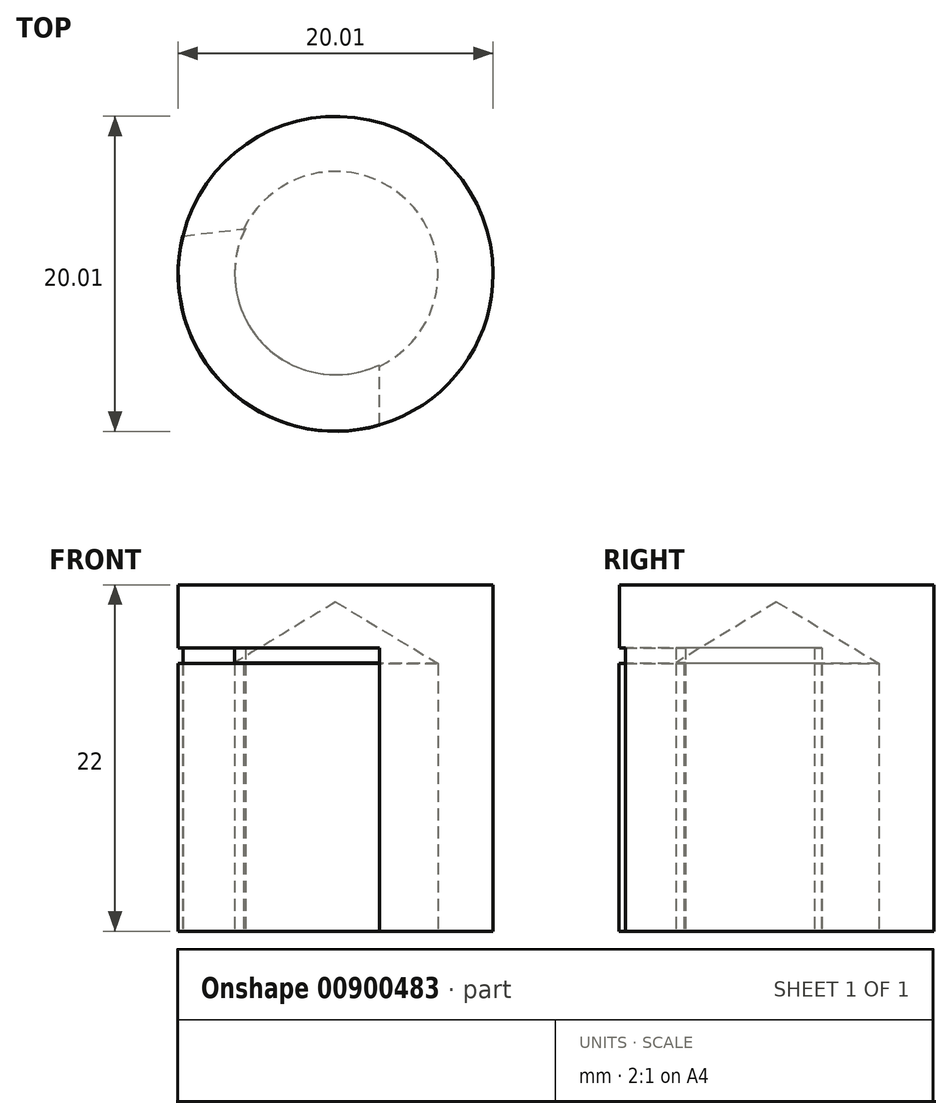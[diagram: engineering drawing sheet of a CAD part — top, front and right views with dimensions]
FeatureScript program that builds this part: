
annotation { "Feature Type Name" : "Feature", "Feature Type Description" : "" }
export const myFeature = defineFeature(function(context is Context, id is Id, definition is map)
    precondition{}
    {
        {
            var Q0;
            Q0=qCreatedBy(makeId("Top.planeOp"),FACE);
            var sketch = newSketch(context, id + "F0", { "sketchPlane" : qUnion([Q0])});
            skCircle(sketch, "E0", {"center": v(0, 0) * mm, "radius": 10 * mm});
            skSolve(sketch);
        }
        {
            var Q0;
            Q0=makeQuery(id+"F0.imprint","IMPRINT",FACE,{"disambiguationData":[TD([[makeQuery(id+"F0.imprint","IMPRINT",EDGE,{"derivedFrom":sQuery(id+"F0.wireOp",EDGE,"E0")}),1.0]])]});
            extrude(context, id + "F1", {"entities" : qUnion([Q0]), "depth" : 22 * mm, "offsetDistance" : 25.4 * mm});
        }
        {
            var Q0;
            Q0=makeQuery(id+"F1.opExtrude","CAP_FACE",FACE,{"disambiguationData":[OSD([sQuery(id+"F0.wireOp",EDGE,"E0")])],"isStart":true});
            var sketch = newSketch(context, id + "F2", { "sketchPlane" : qUnion([Q0])});
            skCircle(sketch, "E1", {"center": v(0, 0) * mm, "radius": 6.5 * mm});
            skSolve(sketch);
        }
        {
            var Q0;
            Q0=sQuery(id+"F2.wireOp",VERTEX,"E1.center");
            var Q1;
            Q1=makeQuery(id+"F1.opExtrude","SWEPT_BODY",BODY,{"disambiguationData":[OSD([sQuery(id+"F0.wireOp",EDGE,"E0")])]});
            hole(context, id + "F3", {"style" : HoleStyle.SIMPLE, "endStyle" : HoleEndStyle.BLIND, "holeDiameter" : 13 * mm, "majorDiameter" : 6.35 * mm, "holeDepth" : 17 * mm, "tappedDepth" : 12.7 * mm, "tapClearance" : 3, "locations" : qUnion([Q0]), "scope" : qUnion([Q1])});
        }
        {
            var Q0;
            Q0=qCreatedBy(makeId("Top.planeOp"),FACE);
            var sketch = newSketch(context, id + "F4", { "sketchPlane" : qUnion([Q0])});
            skArc(sketch, "E2", {"start": v(2.77, -5.78) * mm, "mid": v(-4.57, -4.5) * mm, "end": v(-5.74, 2.86) * mm});
            skArc(sketch, "E3", {"start": v(2.77, -9.62) * mm, "mid": v(-6.94, -7.21) * mm, "end": v(-9.72, 2.4) * mm});
            skLineSegment(sketch, "E4", {"start": v(-9.72, 2.4) * mm, "end": v(-5.74, 2.86) * mm});
            skLineSegment(sketch, "E5", {"start": v(2.77, -9.62) * mm, "end": v(2.77, -5.78) * mm});
            skSolve(sketch);
        }
        {
            var Q0;
            Q0 = qSketchRegion(id + "F4", true);
            extrude(context, id + "F5", {"entities" : qUnion([Q0]), "operationType" : NewBodyOperationType.REMOVE, "depth" : 18 * mm, "offsetDistance" : 25.4 * mm});
        }
        {
            var Q0;
            Q0 = qSketchRegion(id + "F4", true);
            extrude(context, id + "F6", {"entities" : qUnion([Q0]), "operationType" : NewBodyOperationType.ADD, "depth" : 17 * mm, "offsetDistance" : 25.4 * mm});
        }
    });
